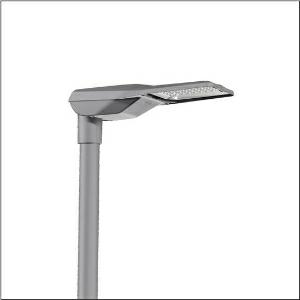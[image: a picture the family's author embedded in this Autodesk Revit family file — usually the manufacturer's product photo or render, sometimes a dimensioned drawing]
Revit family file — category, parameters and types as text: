
# Revit family: streetlight_sl_21_iq_mini___stw1_0a_5xe2e21g08hb_26c4
name_source: partatom
category: Lighting Fixtures
units: mm (PartAtom-declared; Revit-internal decimal feet)

## family parameters
Cut with Voids When Loaded = No
Host = Face
Light Source = No
Part Type = Normal
Room Calculation Point = No
Round Connector Dimension = Use Diameter
Shared = No

## types (1)
- --- (1 x LED, 7830 lm, 70.9 W, 2200K)
    Apparent Load = 71 VA
    CIE Flux Codes = 38 75 98 100 100
    Color Rendering = 70
    Color Temperature = 2200K
    Default Elevation = 1800 mm
    Description = Streetlight SL 21 iQ mini, mast luminaire, primary light control with lens, of PMMA, primary optical cover: cover, of toughened safety glass, transparent, light distribution: STW1.0a, light emission: direct distribution, primary light characteristic: asymmetric, installation type: post-top, side-entry, LED, High Power LED, rated luminous flux: 7.830lm, luminous efficacy: 110lm/W, light colour: 722, colour temperature: 2200K, control gear: iQ Street-Remote, control: Street-Remote, Auto-Match, Temp-Guard, Lumen-Switch, Night-Set, Smart-Wire, Light-Fading, Desk-Remote (wireless, voltage-free reading and setting of iQ features in the workshop via application-optimized NFC function/RFID function), optimised constant luminous flux control (CLO 2.0), pre-setting: linear dimming characteristic, mains connection: 220..240V, AC, 50/60Hz, start of lifetime: 71W, end of service life: 75W, reduction: 31W, luminaire housing, of diecast aluminium, powder-coated, SITECO metallic grey (DB 702S), corrosivity category C5 high according to DIN EN ISO 12944, please order mast flange separately, inclination adjustable: 0°, 5°, 10°, 15°, sealing non-destructively replaceable, multi-level sealing system, length: 628mm, width: 235mm, height: 110mm, mast flange for spigot size: 42mm (side-entry): 5XC10008XM4, 60/48mm (side-entry/post-top): 5XC10108XM2, 76/60mm (side-entry/post-top): 5XC10108XM1, mounting height: 4..8m, protection rating (complete): IP66, insulation class (complete): insulation class II (safety insulation), certification: CE, ENEC, ENEC+, VDE, impact resistance: IK10, permissible operating ambient temperature for outdoor applications: -40..+50°C, standard-compliant lighting for roads and squares, packaging unit: 1 piece

Light Distribution: STW1.0a
    Height = 110 mm
    Lamp = 1 x LED
    Lamp Light Flux = 7830 lm
    Lamp Power = 70.9 W
    Lamp count = 1
    Length = 625 mm
    Luminous efficacy = 110 lm/W
    Manufacturer = Siteco
    ModVariant = No
    Model = 5XE2E21G08HB
    Number of Poles = 1
    OnlyDefault = Yes
    Power Factor = 1
    Product Name = Streetlight SL 21 iQ mini | STW1.0a
    Product group = mast luminaire | pylon top
    ProductGroupID = 6100
    Protection Class = Protection class II
    Protection Degree = IP 66
    RLX_Detail_Level = 1
    RLX_Emergency_Light_Flux = 0 lm
    RLX_Emergency_Type = 0
    RLX_Emergency_Type_DB = No
    RlxData = <blob elided: 26301 chars, md5=08ffca9d>
    Socket = socket
    Standby Power = 0 W
    System Light Flux = 7830 lm
    System Power = 71 W
    Type Comments = factory setting: luminous flux: 100 % | dim-lin: 254 | 711 mA
    Type Image = l_1003519.jpg
    URL = http://relux.com
    VarID = @adj_157451
    Voltage = 0 V
    Weight = 0.00 kg
    Width = 234 mm

## geometry (parser evidence)
native form markers: Blend x4, Sweep x10
no freeform markers — native parametric forms only
